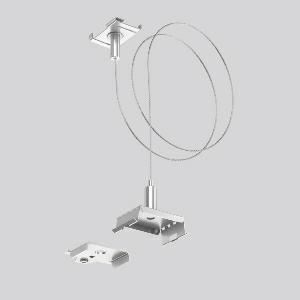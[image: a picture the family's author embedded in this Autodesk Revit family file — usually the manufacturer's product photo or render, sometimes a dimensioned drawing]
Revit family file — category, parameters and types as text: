
# Revit family: linedo_pendelset_5m_seil_caddyclip_982719_000_baf2
name_source: partatom
category: Lighting Fixtures
units: mm (PartAtom-declared; Revit-internal decimal feet)

## family parameters
Cut with Voids When Loaded = No
Host = Face
Light Source = No
Part Type = Normal
Room Calculation Point = No
Round Connector Dimension = Use Diameter
Shared = No

## types (1)
- LINEDO Pendelset 5m Seil Caddyclip
    Apparent Load = 0 VA
    Default Elevation = 1800 mm
    Description = Suspension kit for grid ceilings with steel cable 5,000 mm and caddy clip. Spring steel, blank, for installing continuous line luminaire modules.
Colour: stainless steel
Length: 54 mm
Width: 30 mm
Height: 42 mm
Weight: 265 g
Type of Installation: pendant
    Height = 43 mm
    Lamp = 0 x
    Length = 54 mm
    Luminous efficacy = 0 lm/W
    Manufacturer = RZB
    ModVariant = No
    Model = 982719.000
    Mounting Place = Ceiling
    Mounting Type = Surface mounted
    Number of Poles = 1
    OnlyDefault = Yes
    Power Factor = 1
    Product Name = LINEDO Pendelset 5m Seil Caddyclip
    Product group = Surface mounted continuous line luminaire system
    ProductGroupID = 310
    Protection Class = Protection class
    Protection Degree = Degree of protection
    RLX_Detail_Level = 1
    RLX_Emergency_Light_Flux = 0 lm
    RLX_Emergency_Type = 0
    RLX_Emergency_Type_DB = No
    RlxData = <blob elided: 23957 chars, md5=b2e34403>
    Standby Power = 0 W
    System Light Flux = 0 lm
    System Power = 0 W
    Type Comments = Product without accessories
    Type Image = 982719.000.jpg
    URL = http://relux.com
    VarID = ---
    Voltage = 0 V
    Weight = 0.00 kg
    Width = 30 mm  [stored 0.0984252 ft]

note: [stored X ft] marks values corroborated as IEEE doubles in the binary element streams (Revit-internal decimal feet)

## geometry (parser evidence)
native form markers: Blend x4, Sweep x11
no freeform markers — native parametric forms only
